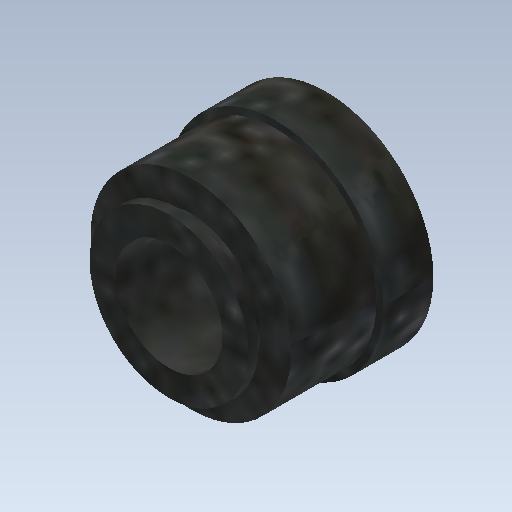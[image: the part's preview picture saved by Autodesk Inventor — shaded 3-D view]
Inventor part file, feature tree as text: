
AUTODESK INVENTOR PART (.ipt)
format: ipt  version: 2020 (Build 240168000, 168)  size: 219,136 bytes
history: native  units: mm
features: revolve x2, sketch x2, projected_geometry x1
ambient origin geometry x8: Origin, YZ Plane, XZ Plane, XY Plane, X Axis, Y Axis, Z Axis, Center Point
bodies: Solid1 (feature_tree)
feature tree (5):
  revolve  "Revolution1"  [1 undecoded]
  revolve  "Revolution2"  [1 undecoded]
  sketch  "Sketch1"  dims[d0=5.0mm d1=10.4mm]
  sketch  "Sketch3"  dims[d2=1.0mm d3=0.0mm d4=3.0mm d5=7.41mm d6=1.7mm d8=6.0mm d9=6.408039mm d10=3.2mm d11=90.0deg d13=0.6mm d14=1.3mm d15=4.15mm d16=4.75mm d17=90.0deg]
  projected_geometry  "Project Cut Edges1"
note: 2 required parameter values undecoded (feature->parameter linkage not recoverable at this tier; creation-order binding heuristic only, values carry confidence <= 0.55)
